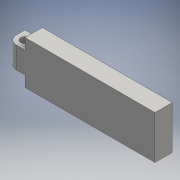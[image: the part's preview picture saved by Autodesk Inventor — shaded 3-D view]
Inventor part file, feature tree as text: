
AUTODESK INVENTOR PART (.ipt)
format: ipt  version: 2016 (Build 200138000, 138)  size: 105,472 bytes
history: native  units: mm
features: extrude x2, other x1, fillet x1, sketch x1
ambient origin geometry x8: Origin, YZ Plane, XZ Plane, XY Plane, X Axis, Y Axis, Z Axis, Center Point
bodies: Body1 (feature_tree)
feature tree (5):
  other  "ソリッド1"
  extrude  "押し出し1"  Depth=30.0mm
  extrude  "押し出し2"  Depth=10.0mm
  fillet  "フィレット1"  Radius=4.0mm
  sketch  "スケッチ2"
